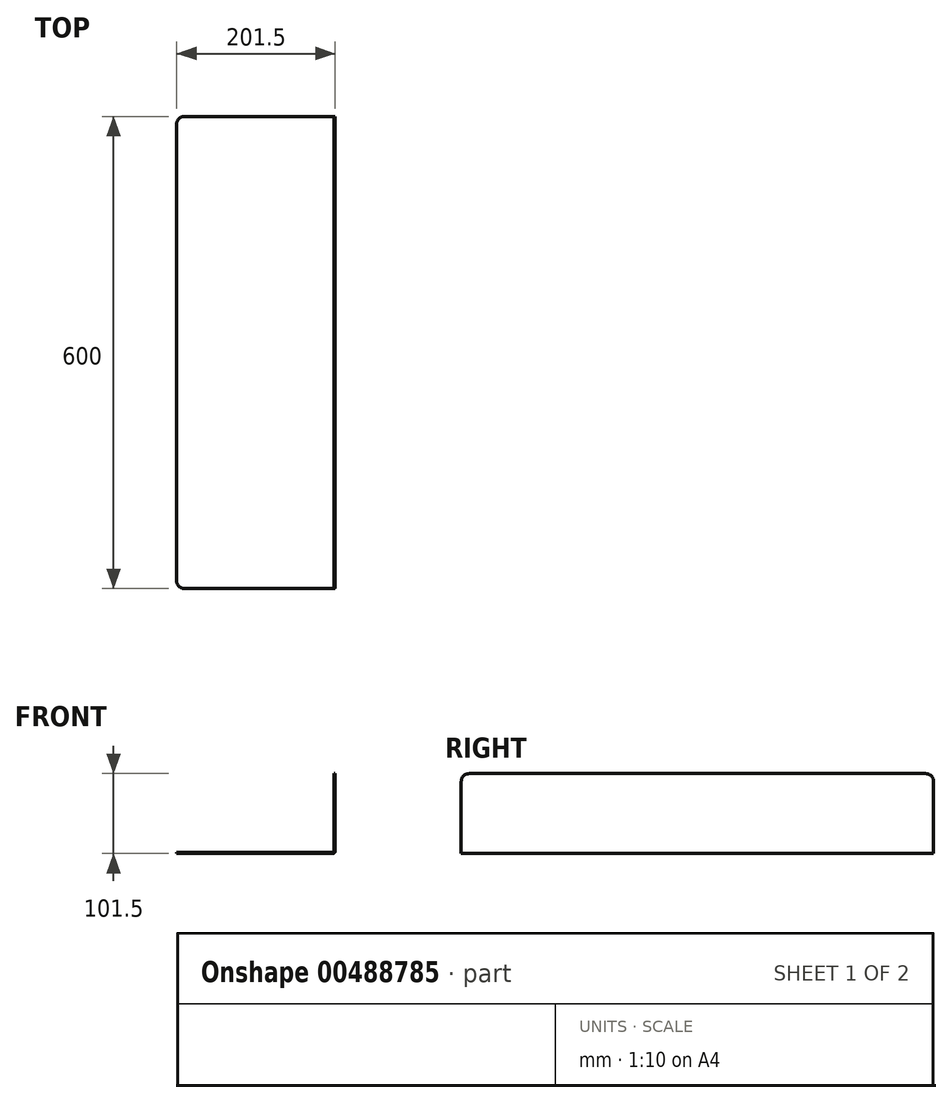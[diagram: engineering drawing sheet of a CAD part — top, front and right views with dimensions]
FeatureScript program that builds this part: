
annotation { "Feature Type Name" : "Feature", "Feature Type Description" : "" }
export const myFeature = defineFeature(function(context is Context, id is Id, definition is map)
    precondition{}
    {
        {
            var Q0;
            Q0=qCreatedBy(makeId("Front.planeOp"),FACE);
            var sketch = newSketch(context, id + "F0", { "sketchPlane" : qUnion([Q0])});
            skLineSegment(sketch, "E0", {"start": v(-201.5, 0) * mm, "end": v(-3.5, 0) * mm});
            skLineSegment(sketch, "E1", {"start": v(0, 3.5) * mm, "end": v(0, 101.5) * mm});
            skLineSegment(sketch, "E2", {"start": v(0, 101.5) * mm, "end": v(-1.5, 101.5) * mm});
            skLineSegment(sketch, "E3", {"start": v(-1.5, 101.5) * mm, "end": v(-1.5, 3.5) * mm});
            skLineSegment(sketch, "E4", {"start": v(-3.5, 1.5) * mm, "end": v(-201.5, 1.5) * mm});
            skLineSegment(sketch, "E5", {"start": v(-201.5, 1.5) * mm, "end": v(-201.5, 0) * mm});
            skArc(sketch, "E6.filletArc", {"start": v(-3.5, 1.5) * mm, "mid": v(-2.09, 2.09) * mm, "end": v(-1.5, 3.5) * mm});
            skPoint(sketch, "E7.visualSharp", {"position": v(0, 0) * mm});
            skArc(sketch, "E7.filletArc", {"start": v(-3.5, 0) * mm, "mid": v(-1.03, 1.03) * mm, "end": v(0, 3.5) * mm});
            skSolve(sketch);
        }
        {
            var Q0;
            Q0 = qSketchRegion(id + "F0", true);
            extrude(context, id + "F1", {"entities" : qUnion([Q0]), "endBound" : BoundingType.SYMMETRIC, "depth" : 600 * mm});
        }
        {
            var Q0;
            Q0=makeQuery(id+"F1.opExtrude","CAP_EDGE",EDGE,{"disambiguationData":[OSD([sQuery(id+"F0.wireOp",EDGE,"E2")])],"isStart":false});
            var Q1;
            Q1=makeQuery(id+"F1.opExtrude","CAP_EDGE",EDGE,{"disambiguationData":[OSD([sQuery(id+"F0.wireOp",EDGE,"E2")])],"isStart":true});
            var Q2;
            Q2=makeQuery(id+"F1.opExtrude","CAP_EDGE",EDGE,{"disambiguationData":[OSD([sQuery(id+"F0.wireOp",EDGE,"E5")])],"isStart":false});
            var Q3;
            Q3=makeQuery(id+"F1.opExtrude","CAP_EDGE",EDGE,{"disambiguationData":[OSD([sQuery(id+"F0.wireOp",EDGE,"E5")])],"isStart":true});
            fillet(context, id + "F2", {"entities" : qUnion([Q0, Q1, Q2, Q3]), "radius" : 10 * mm, "tangentPropagation" : true, "allowEdgeOverflow" : false});
        }
    });
